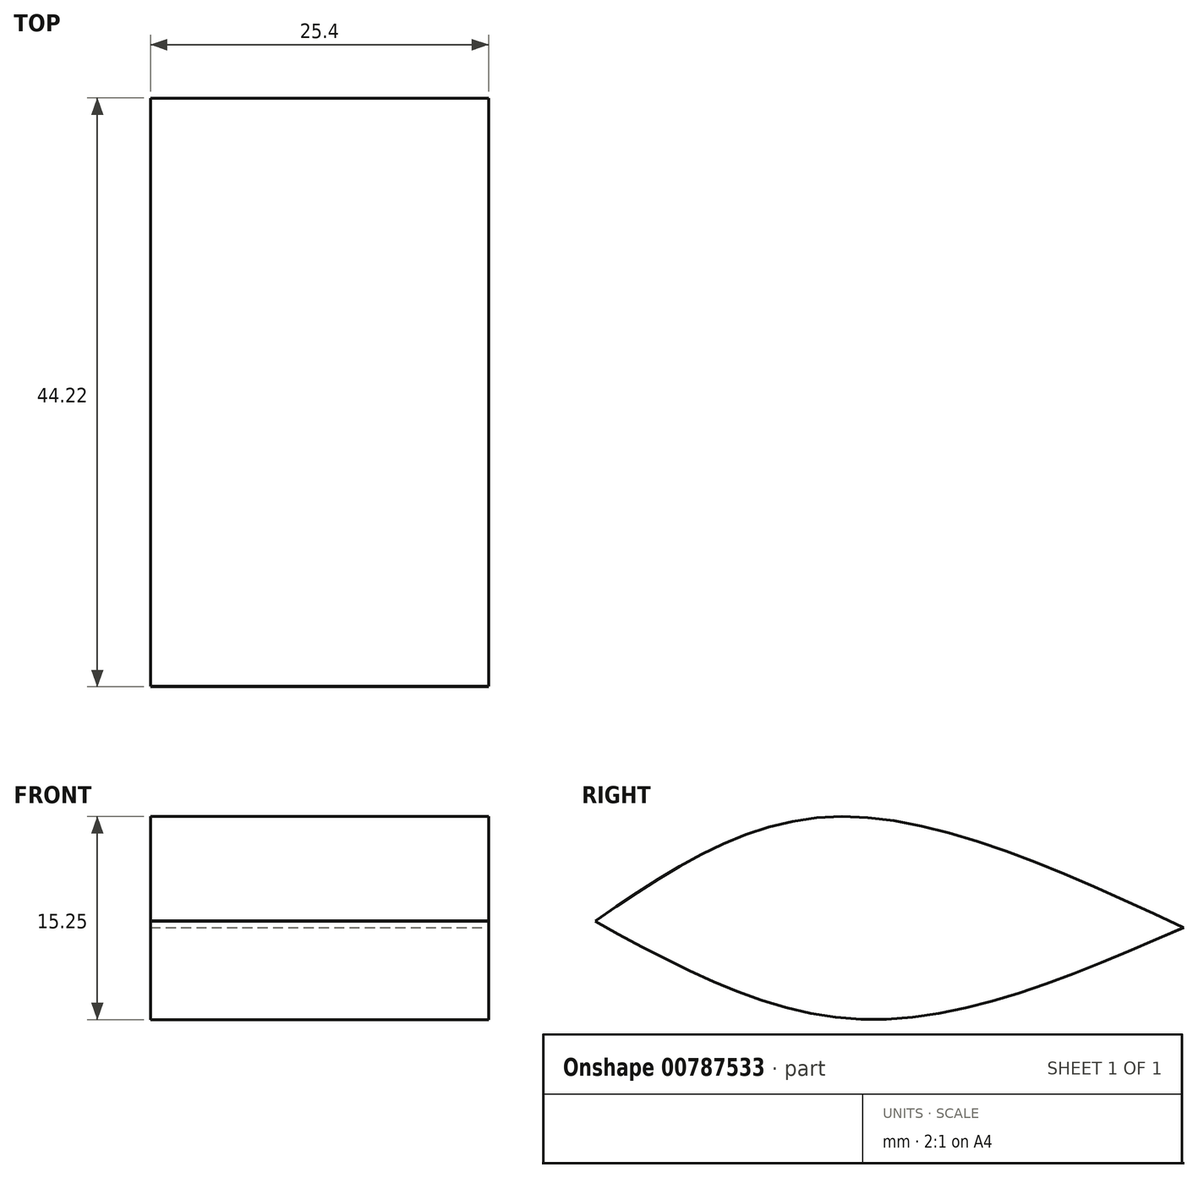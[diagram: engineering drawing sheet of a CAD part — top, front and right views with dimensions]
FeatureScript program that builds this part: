
annotation { "Feature Type Name" : "Feature", "Feature Type Description" : "" }
export const myFeature = defineFeature(function(context is Context, id is Id, definition is map)
    precondition{}
    {
        {
            var Q0;
            Q0=qCreatedBy(makeId("Right.planeOp"),FACE);
            var sketch = newSketch(context, id + "F0", { "sketchPlane" : qUnion([Q0])});
            skFitSpline(sketch, "E0", {"points": [v(-18.24, 11.61) * mm, v(-0.94, 19.4) * mm, v(25.94, 11.1) * mm], "startDerivative": vector(35.98, 24.55) * mm, "endDerivative": vector(51.85, -23.99) * mm});
            skSolve(sketch);
        }
        {
            var Q0;
            Q0=qCreatedBy(makeId("Right.planeOp"),FACE);
            var sketch = newSketch(context, id + "F1", { "sketchPlane" : qUnion([Q0])});
            skFitSpline(sketch, "E1", {"points": [v(-18.28, 11.56) * mm, v(1.74, 4.2) * mm, v(25.94, 11.1) * mm], "startDerivative": vector(40.63, -22.22) * mm, "endDerivative": vector(47.7, 20.7) * mm});
            skSolve(sketch);
        }
        {
            var Q0;
            Q0=sQuery(id+"F1.wireOp",EDGE,"E1");
            var Q1;
            Q1=sQuery(id+"F0.wireOp",EDGE,"E0");
            extrude(context, id + "F2", {"bodyType" : ToolBodyType.SURFACE, "surfaceEntities" : qUnion([Q0, Q1]), "depth" : 25.4 * mm, "offsetDistance" : 25.4 * mm});
        }
    });
